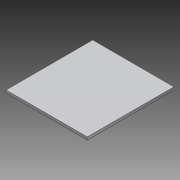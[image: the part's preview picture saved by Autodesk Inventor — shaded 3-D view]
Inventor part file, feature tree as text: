
AUTODESK INVENTOR PART (.ipt)
format: ipt  version: 2014 SP1 (Build 180222100, 222)  size: 69,632 bytes
history: native  units: in
note: dims shown in document units (in); Inventor stores cm internally (conversion verified against a paired STEP export)
features: extrude x1, sketch x1
ambient origin geometry x8: Origin, YZ Plane, XZ Plane, XY Plane, X Axis, Y Axis, Z Axis, Center Point
bodies: Solid1 (feature_tree)
feature tree (2):
  extrude  "Extrusion1"  Depth=2.0in
  sketch  "Sketch1"  dims[d0=1.875in d1=2.0in d2=0.0625in d3=0.0in]
